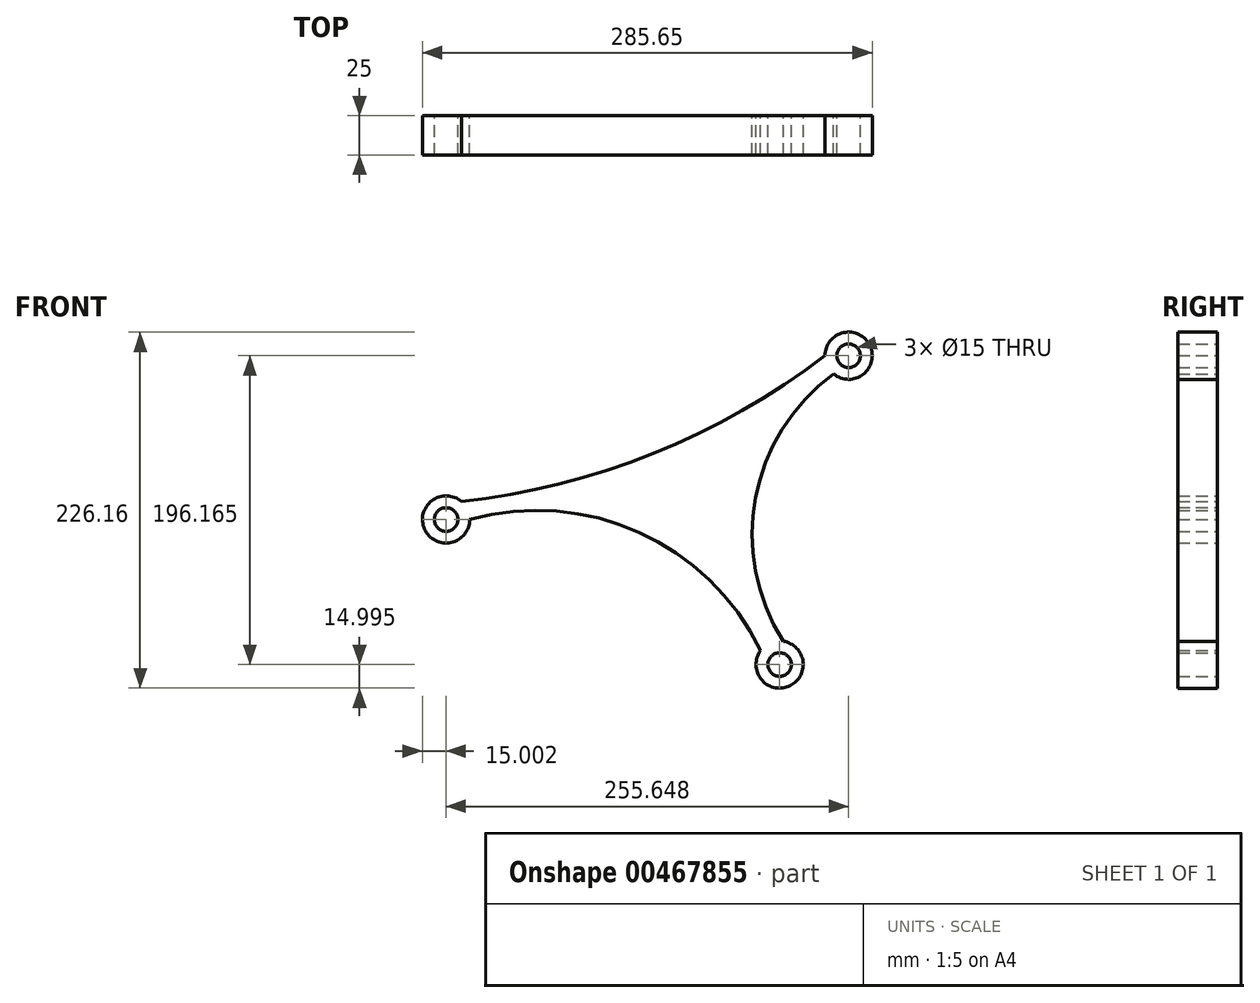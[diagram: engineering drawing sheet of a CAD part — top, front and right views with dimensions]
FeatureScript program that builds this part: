
annotation { "Feature Type Name" : "Feature", "Feature Type Description" : "" }
export const myFeature = defineFeature(function(context is Context, id is Id, definition is map)
    precondition{}
    {
        {
            var Q0;
            Q0=qCreatedBy(makeId("Front.planeOp"),FACE);
            var sketch = newSketch(context, id + "F0", { "sketchPlane" : qUnion([Q0])});
            skCircle(sketch, "E0", {"center": v(0, 0) * mm, "radius": 15 * mm});
            skCircle(sketch, "E1", {"center": v(0, 0) * mm, "radius": 7.5 * mm});
            skCircle(sketch, "E2", {"center": v(-255.65, -104.02) * mm, "radius": 15 * mm});
            skCircle(sketch, "E3", {"center": v(-255.65, -104.02) * mm, "radius": 7.5 * mm});
            skCircle(sketch, "E4", {"center": v(-43.82, -196.16) * mm, "radius": 15 * mm});
            skCircle(sketch, "E5", {"center": v(-43.82, -196.16) * mm, "radius": 7.5 * mm});
            skArc(sketch, "E6", {"start": v(-55.9, -187.27) * mm, "mid": v(-133.2, -112.17) * mm, "end": v(-240.65, -104.02) * mm});
            skArc(sketch, "E7", {"start": v(-9.51, -11.6) * mm, "mid": v(-59.07, -90.16) * mm, "end": v(-41.42, -181.36) * mm});
            skArc(sketch, "E8", {"start": v(-245.88, -92.63) * mm, "mid": v(-124.11, -62.1) * mm, "end": v(-15, 0) * mm});
            skSolve(sketch);
        }
        {
            var Q0;
            Q0 = qSketchRegion(id + "F0", true);
            extrude(context, id + "F1", {"entities" : qUnion([Q0]), "depth" : 25 * mm});
        }
    });
